# Revit family: Selector Valve -JCI_Sapphire_Plus-(140bar)Novec1230-Manual Release
name_source: partatom
category: Specialty Equipment
revit_build: Autodesk Revit 2017 (Build: 20171027_0315(x64)
units: mm (PartAtom-declared; Revit-internal decimal feet)

## family parameters
Always vertical = No
Cut with Voids When Loaded = No
OmniClass Number = 23.29.33.13.11
Part Type = Normal
Room Calculation Point = No
Round Connector Dimension = Use Diameter
Shared = Yes
Work Plane-Based = Yes

## types (8) — shared parameters
Assembly Code = D4090300
Date Modified = YYYY/MM/DD
Diameter = 47.6 mm  [stored 0.156168 ft]
Discharge Flow = 0 GPM
Equipment Abbreviation = SV
Equipment Tag = XXX
Family Version = 1.0
Fire Suppression Agent = 3M™ Novec™ 1230 Fire Protection Fluid
Length = 47.6 mm  [stored 0.156168 ft]
Manufacturer = Johnson Controls, Inc.
Material = JCI - Metal - Brass - Satin
Model Disclaimer = For More Information Contact JOHNSON CONTROLS
Product Documentation Link = http://www.sapphireplus.com
Product Page URL = http://www.sapphireplus.com
URL = http://www.sapphireplus.com
Width = 47.6 mm  [stored 0.156168 ft]
zero-valued in all types: Default Elevation

## per-type parameters (varying)
| type | B | C | D | Description | Height | Model | PD | Part Description | Part Number | Pipe Diameter | X | X1 | X2 | Y |
| 20mm (3/4in) With 6 mm Tube Fitting | 6 mm  [stored 0.019685 ft] | 230 mm | 50 mm  [stored 0.164042 ft] | 20mm (3/4in) With 6 mm Tube Fitting | 511 mm | 445043 | 15 mm  [stored 0.0492126 ft] | 20mm (3/4in) With 6 mm Tube Fitting | 445043 | 30 mm  [stored 0.0984252 ft] | 41 mm  [stored 0.134514 ft] | 17 mm | 31 mm  [stored 0.101706 ft] | 60 mm  [stored 0.19685 ft] |
| 100mm (4in) With 6 mm Tube Fitting | 16 mm  [stored 0.0524934 ft] | 291 mm | 111 mm | 100mm (4in) With 6 mm Tube Fitting | 748 mm | 445050 | 50 mm  [stored 0.164042 ft] | 100mm (4in) With 6 mm Tube Fitting | 445050 | 100 mm  [stored 0.328084 ft] | 102.5 mm | 41 mm  [stored 0.134514 ft] | 70 mm  [stored 0.229659 ft] | 120 mm |
| 25mm (1in) With 6 mm Tube Fitting | 8 mm  [stored 0.0262467 ft] | 233 mm | 54 mm  [stored 0.177165 ft] | 25mm (1in) With 6 mm Tube Fitting | 524 mm | 445044 | 15 mm  [stored 0.0492126 ft] | 25mm (1in) With 6 mm Tube Fitting | 445044 | 30 mm  [stored 0.0984252 ft] | 45 mm  [stored 0.147638 ft] | 21 mm  [stored 0.0688976 ft] | 35 mm  [stored 0.114829 ft] | 60 mm  [stored 0.19685 ft] |
| 32mm (1 1/4in) With 6 mm Tube Fitting | 13 mm | 233 mm | 54 mm  [stored 0.177165 ft] | 32mm (1 1/4in) With 6 mm Tube Fitting | 527 mm | 445045 | 21 mm  [stored 0.0688976 ft] | 32mm (1 1/4in) With 6 mm Tube Fitting | 445045 | 42 mm  [stored 0.137795 ft] | 55 mm  [stored 0.180446 ft] | 22 mm  [stored 0.0721785 ft] | 35 mm  [stored 0.114829 ft] | 60 mm  [stored 0.19685 ft] |
| 40mm (1 1/2in) With 6 mm Tube Fitting | 15 mm  [stored 0.0492126 ft] | 230 mm | 62 mm  [stored 0.203412 ft] | 40mm (1 1/2in) With 6 mm Tube Fitting | 543 mm | 445046 | 23 mm  [stored 0.0754593 ft] | 40mm (1 1/2in) With 6 mm Tube Fitting | 445046 | 46 mm  [stored 0.150919 ft] | 61 mm  [stored 0.200131 ft] | 26 mm | 40 mm  [stored 0.131234 ft] | 60 mm  [stored 0.19685 ft] |
| 50mm (2in) With 6 mm Tube Fitting | 14 mm  [stored 0.0459318 ft] | 230 mm | 77 mm  [stored 0.252625 ft] | 50mm (2in) With 6 mm Tube Fitting | 560 mm | 445047 | 29 mm  [stored 0.0951444 ft] | 50mm (2in) With 6 mm Tube Fitting | 445047 | 58 mm  [stored 0.190289 ft] | 70 mm  [stored 0.229659 ft] | 30 mm  [stored 0.0984252 ft] | 40 mm  [stored 0.131234 ft] | 60 mm  [stored 0.19685 ft] |
| 65mm (2 1/2in) With 6 mm Tube Fitting | 16 mm  [stored 0.0524934 ft] | 230 mm | 86 mm  [stored 0.282152 ft] | 65mm (2 1/2in) With 6 mm Tube Fitting | 590 mm | 445048 | 35 mm  [stored 0.114829 ft] | 65mm (2 1/2in) With 6 mm Tube Fitting | 445048 | 70 mm  [stored 0.229659 ft] | 85 mm  [stored 0.278871 ft] | 40 mm  [stored 0.131234 ft] | 47 mm  [stored 0.154199 ft] | 85 mm  [stored 0.278871 ft] |
| 80mm (3 in) With 6 mm Tube Fitting | 17 mm | 230 mm | 95 mm | 80mm (3in) With 6 mm Tube Fitting | 612 mm | 445049 | 42 mm  [stored 0.137795 ft] | 80mm (3in) With 6 mm Tube Fitting | 445049 | 84 mm  [stored 0.275591 ft] | 105 mm  [stored 0.344488 ft] | 42 mm  [stored 0.137795 ft] | 52 mm | 85 mm  [stored 0.278871 ft] |

note: [stored X ft] marks values corroborated as IEEE doubles in the binary element streams (Revit-internal decimal feet)

## geometry (parser evidence)
native form markers: Sweep x1
no freeform markers — native parametric forms only
